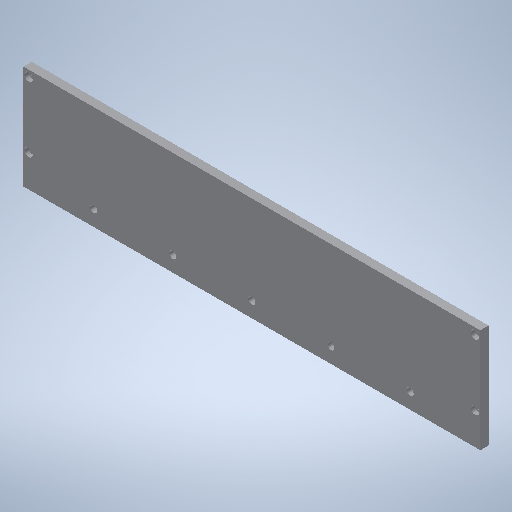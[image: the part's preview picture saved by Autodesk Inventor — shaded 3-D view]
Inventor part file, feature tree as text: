
AUTODESK INVENTOR PART (.ipt)
format: ipt  version: 2025 (Build 290162000, 162)  size: 268,288 bytes
history: native  units: in
note: dims shown in document units (in); Inventor stores cm internally (conversion verified against a paired STEP export)
features: sketch x4, hole x2, extrude x1
ambient origin geometry x8: Origin, YZ Plane, XZ Plane, XY Plane, X Axis, Y Axis, Z Axis, Center Point
bodies: Solid1 (feature_tree)
feature tree (7):
  extrude  "Extrusion1"  Depth=17.3228in
  hole  "Hole1"  [1 undecoded]
  hole  "Hole2"  [1 undecoded]
  sketch  "Sketch1"  dims[d0=3.937in d1=17.3228in]
  sketch  "Sketch2"  dims[d6=0.1969in d7=0.1969in]
  sketch  "Sketch3"  dims[d8=0.1693in d9=0.75in d10=0.315in d11=0.1575in d12=0.5635in d13=1.0in d14=0.8108in d15=2.6614in d16=0.5906in d19=0.266in d20=0.75in d21=0.438in d22=0.15in d23=0.5635in d24=1.0in d25=0.8108in d38=1.9685in d40=3.0in d41=0.3937in d43=0.3937in d45=17.3228in d46=2.7165in]
  sketch  "Sketch Rectangular Pattern1"  dims[d2=0.315in d3=0.0in d5=0.2362in]
note: 2 required parameter values undecoded (feature->parameter linkage not recoverable at this tier; creation-order binding heuristic only, values carry confidence <= 0.55)
